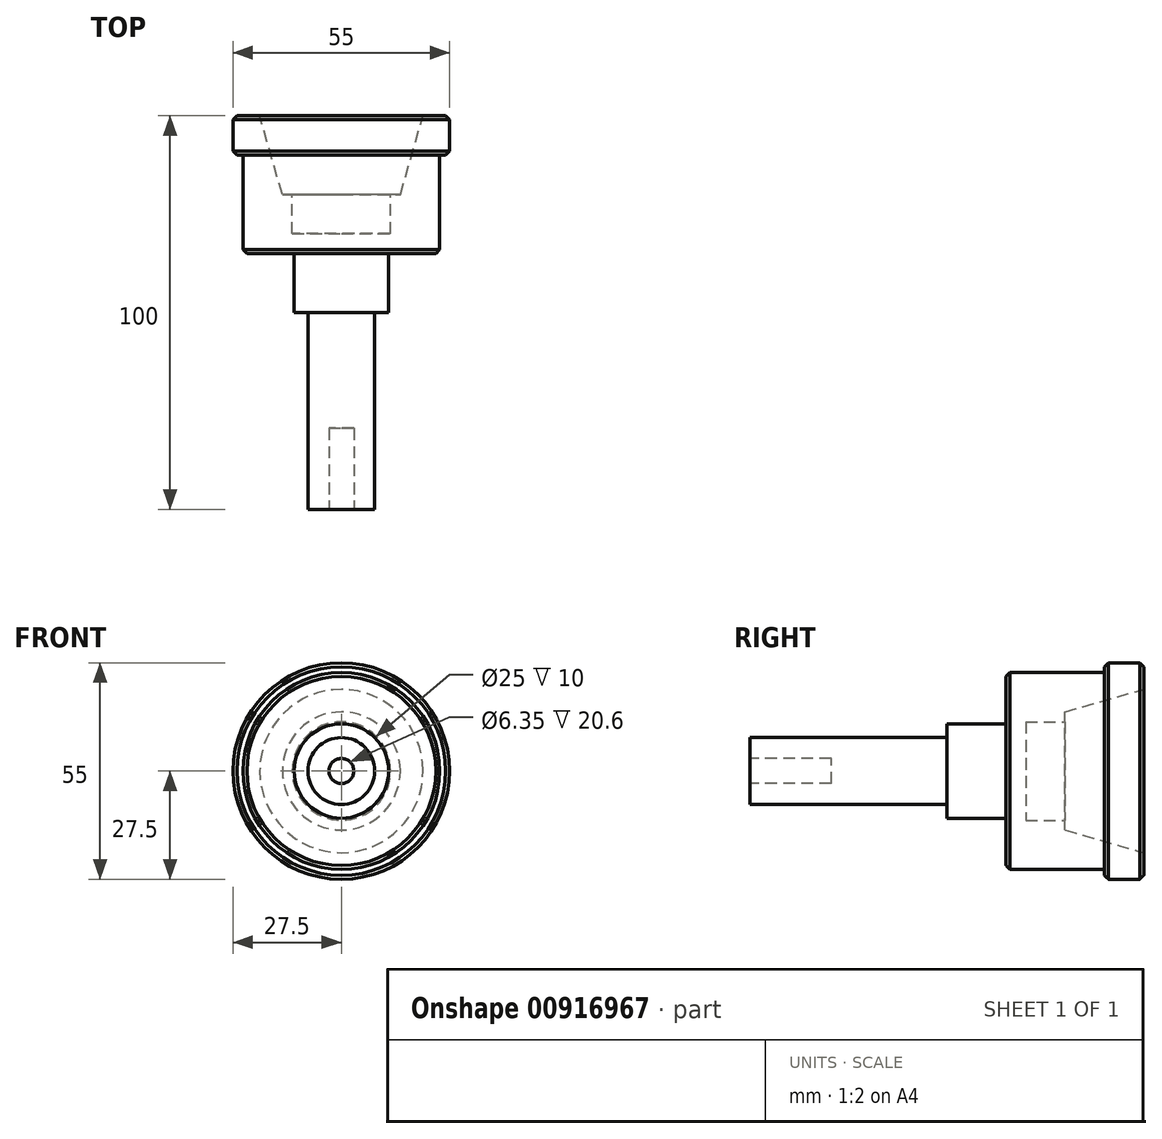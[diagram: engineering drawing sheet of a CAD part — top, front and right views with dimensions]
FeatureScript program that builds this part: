
annotation { "Feature Type Name" : "Feature", "Feature Type Description" : "" }
export const myFeature = defineFeature(function(context is Context, id is Id, definition is map)
    precondition{}
    {
        {
            var Q0;
            Q0=qCreatedBy(makeId("Front.planeOp"),FACE);
            var sketch = newSketch(context, id + "F0", { "sketchPlane" : qUnion([Q0])});
            skCircle(sketch, "E0", {"center": v(0, 0) * mm, "radius": 27.5 * mm});
            skSolve(sketch);
        }
        {
            var Q0;
            Q0=makeQuery(id+"F0.imprint","IMPRINT",FACE,{"disambiguationData":[TD([[makeQuery(id+"F0.imprint","IMPRINT",EDGE,{"derivedFrom":sQuery(id+"F0.wireOp",EDGE,"E0")}),1.0]])]});
            extrude(context, id + "F1", {"entities" : qUnion([Q0]), "depth" : 10 * mm, "offsetDistance" : 25 * mm});
        }
        {
            var Q0;
            Q0=makeQuery(id+"F1.opExtrude","CAP_FACE",FACE,{"disambiguationData":[OSD([sQuery(id+"F0.wireOp",EDGE,"E0")])],"isStart":false});
            var sketch = newSketch(context, id + "F2", { "sketchPlane" : qUnion([Q0])});
            skCircle(sketch, "E1", {"center": v(0, 0) * mm, "radius": 25 * mm});
            skSolve(sketch);
        }
        {
            var Q0;
            Q0=makeQuery(id+"F2.imprint","IMPRINT",FACE,{"disambiguationData":[TD([[makeQuery(id+"F2.imprint","IMPRINT",EDGE,{"derivedFrom":sQuery(id+"F2.wireOp",EDGE,"E1")}),1.0]])]});
            extrude(context, id + "F3", {"entities" : qUnion([Q0]), "operationType" : NewBodyOperationType.ADD, "depth" : 25 * mm, "offsetDistance" : 25 * mm});
        }
        {
            var Q0;
            Q0=makeQuery(id+"F3.opExtrude","CAP_FACE",FACE,{"disambiguationData":[OSD([sQuery(id+"F2.wireOp",EDGE,"E1")])],"isStart":false});
            var sketch = newSketch(context, id + "F4", { "sketchPlane" : qUnion([Q0])});
            skCircle(sketch, "E2", {"center": v(0, 0) * mm, "radius": 12 * mm});
            skSolve(sketch);
        }
        {
            var Q0;
            Q0=makeQuery(id+"F4.imprint","IMPRINT",FACE,{"disambiguationData":[TD([[makeQuery(id+"F4.imprint","IMPRINT",EDGE,{"derivedFrom":sQuery(id+"F4.wireOp",EDGE,"E2")}),1.0]])]});
            extrude(context, id + "F5", {"entities" : qUnion([Q0]), "operationType" : NewBodyOperationType.ADD, "depth" : 15 * mm, "offsetDistance" : 25 * mm});
        }
        {
            var Q0;
            Q0=makeQuery(id+"F1.opExtrude","CAP_EDGE",EDGE,{"disambiguationData":[OSD([sQuery(id+"F0.wireOp",EDGE,"E0")])],"isStart":false});
            var Q1;
            Q1=makeQuery(id+"F1.opExtrude","CAP_EDGE",EDGE,{"disambiguationData":[OSD([sQuery(id+"F0.wireOp",EDGE,"E0")])],"isStart":true});
            var Q2;
            Q2=makeQuery(id+"F3.opExtrude","CAP_EDGE",EDGE,{"disambiguationData":[OSD([sQuery(id+"F2.wireOp",EDGE,"E1")])],"isStart":false});
            chamfer(context, id + "F6", {"entities" : qUnion([Q0, Q1, Q2]), "width" : 1 * mm, "tangentPropagation" : true});
        }
        {
            var Q0;
            Q0=qCreatedBy(makeId("Top.planeOp"),FACE);
            var sketch = newSketch(context, id + "F7", { "sketchPlane" : qUnion([Q0])});
            skLineSegment(sketch, "E3", {"start": v(0, 0) * mm, "end": v(0, -20) * mm});
            skLineSegment(sketch, "E4", {"start": v(0, -20) * mm, "end": v(15, -20) * mm});
            skLineSegment(sketch, "E5", {"start": v(0, 0) * mm, "end": v(20.75, 0) * mm});
            skLineSegment(sketch, "E6", {"start": v(20.75, 0) * mm, "end": v(15, -20) * mm});
            skSolve(sketch);
        }
        {
            var Q0;
            Q0=makeQuery(id+"F7.imprint","IMPRINT",FACE,{"disambiguationData":[TD([[makeQuery(id+"F7.imprint","IMPRINT",EDGE,{"derivedFrom":sQuery(id+"F7.wireOp",EDGE,"E3")}),1.0]])]});
            var Q1;
            Q1=sQuery(id+"F7.wireOp",EDGE,"E3");
            revolve(context, id + "F8", {"operationType" : NewBodyOperationType.REMOVE, "surfaceOperationType" : NewSurfaceOperationType.NEW, "entities" : qUnion([Q0]), "axis" : qUnion([Q1]), "revolveType" : RevolveType.FULL, "oppositeDirection" : true});
        }
        {
            var Q0;
            Q0=makeQuery(id+"F8.boolean.opBoolean","COPY",FACE,{"derivedFrom":makeQuery(id+"F8.opRevolve","SWEPT_FACE",FACE,{"disambiguationData":[OSD([sQuery(id+"F7.wireOp",EDGE,"E4")])]})});
            var sketch = newSketch(context, id + "F9", { "sketchPlane" : qUnion([Q0])});
            skCircle(sketch, "E7", {"center": v(0, 0) * mm, "radius": 12.5 * mm});
            skSolve(sketch);
        }
        {
            var Q0;
            Q0=makeQuery(id+"F9.imprint","IMPRINT",FACE,{"disambiguationData":[TD([[makeQuery(id+"F9.imprint","IMPRINT",EDGE,{"derivedFrom":sQuery(id+"F9.wireOp",EDGE,"E7")}),1.0]])]});
            extrude(context, id + "F10", {"entities" : qUnion([Q0]), "operationType" : NewBodyOperationType.REMOVE, "oppositeDirection" : true, "depth" : 10 * mm, "offsetDistance" : 25 * mm});
        }
        {
            var Q0;
            Q0=makeQuery(id+"F5.opExtrude","CAP_FACE",FACE,{"disambiguationData":[OSD([sQuery(id+"F4.wireOp",EDGE,"E2")])],"isStart":false});
            var sketch = newSketch(context, id + "F11", { "sketchPlane" : qUnion([Q0])});
            skCircle(sketch, "E8", {"center": v(0, 0) * mm, "radius": 8.5 * mm});
            skSolve(sketch);
        }
        {
            var Q0;
            Q0=makeQuery(id+"F11.imprint","IMPRINT",FACE,{"disambiguationData":[TD([[makeQuery(id+"F11.imprint","IMPRINT",EDGE,{"derivedFrom":sQuery(id+"F11.wireOp",EDGE,"E8")}),1.0]])]});
            extrude(context, id + "F12", {"entities" : qUnion([Q0]), "operationType" : NewBodyOperationType.ADD, "depth" : 50 * mm, "offsetDistance" : 25 * mm});
        }
        {
            var Q0;
            Q0=makeQuery(id+"F12.opExtrude","CAP_FACE",FACE,{"disambiguationData":[OSD([sQuery(id+"F11.wireOp",EDGE,"E8")])],"isStart":false});
            var sketch = newSketch(context, id + "F13", { "sketchPlane" : qUnion([Q0])});
            skCircle(sketch, "E9", {"center": v(0, 0) * mm, "radius": 3.17 * mm});
            skSolve(sketch);
        }
        {
            var Q0;
            Q0=makeQuery(id+"F13.imprint","IMPRINT",FACE,{"disambiguationData":[TD([[makeQuery(id+"F13.imprint","IMPRINT",EDGE,{"derivedFrom":sQuery(id+"F13.wireOp",EDGE,"E9")}),1.0]])]});
            extrude(context, id + "F14", {"entities" : qUnion([Q0]), "operationType" : NewBodyOperationType.REMOVE, "oppositeDirection" : true, "depth" : 20.6 * mm, "offsetDistance" : 25 * mm});
        }
    });
